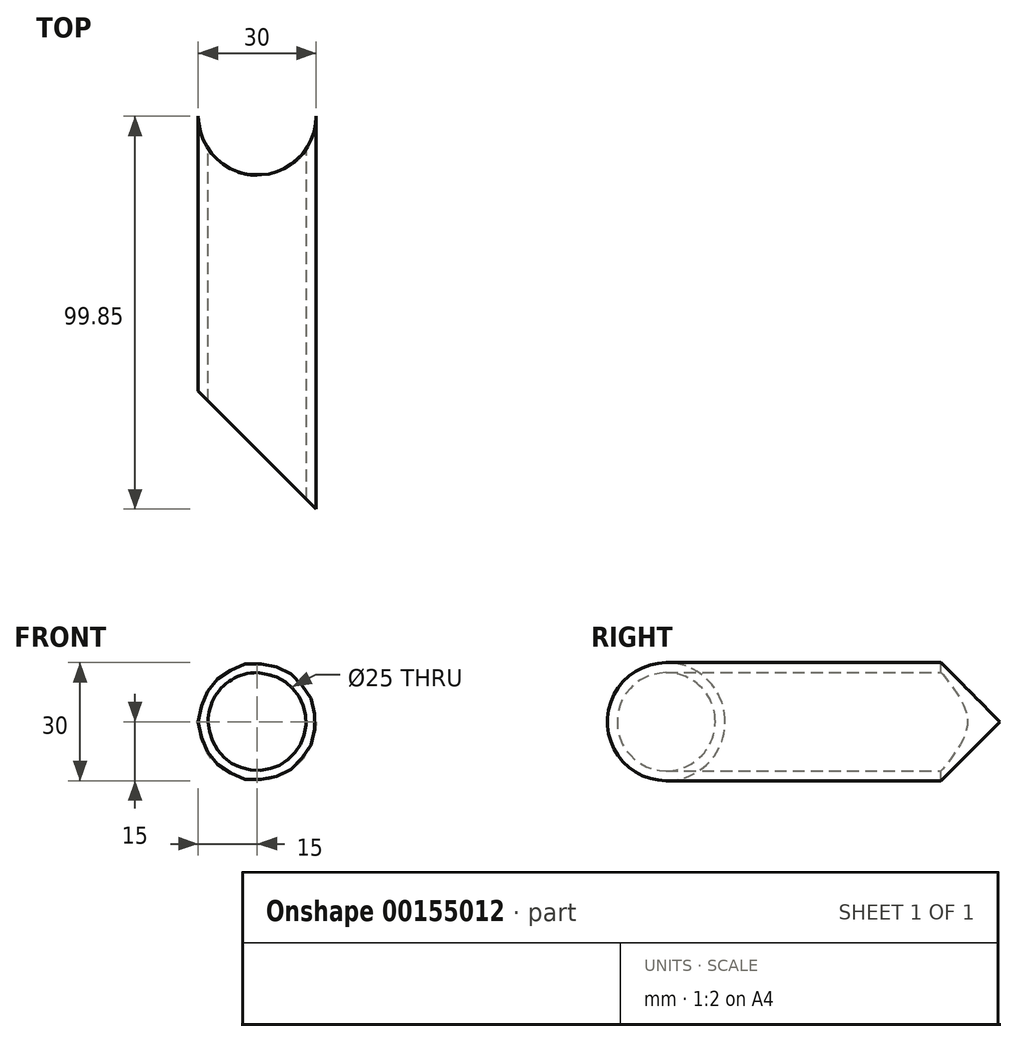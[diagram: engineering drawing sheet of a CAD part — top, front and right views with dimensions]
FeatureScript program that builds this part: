
annotation { "Feature Type Name" : "Feature", "Feature Type Description" : "" }
export const myFeature = defineFeature(function(context is Context, id is Id, definition is map)
    precondition{}
    {
        {
            var Q0;
            Q0=qCreatedBy(makeId("Front.planeOp"),FACE);
            var sketch = newSketch(context, id + "F0", { "sketchPlane" : qUnion([Q0])});
            skCircle(sketch, "E0", {"center": v(0, 0) * mm, "radius": 15 * mm});
            skCircle(sketch, "E1", {"center": v(0, 0) * mm, "radius": 12.5 * mm});
            skSolve(sketch);
        }
        {
            var Q0;
            Q0 = qSketchRegion(id + "F0", true);
            extrude(context, id + "F1", {"entities" : qUnion([Q0]), "depth" : 99.85 * mm});
        }
        {
            var Q0;
            Q0=qCreatedBy(makeId("Top.planeOp"),FACE);
            var sketch = newSketch(context, id + "F2", { "sketchPlane" : qUnion([Q0])});
            skCircle(sketch, "E2", {"center": v(0, 0) * mm, "radius": 15 * mm});
            skSolve(sketch);
        }
        {
            var Q0;
            Q0 = qSketchRegion(id + "F2", true);
            extrude(context, id + "F3", {"entities" : qUnion([Q0]), "operationType" : NewBodyOperationType.REMOVE, "endBound" : BoundingType.SYMMETRIC, "oppositeDirection" : true, "depth" : 35 * mm});
        }
        {
            var Q0;
            Q0=qCreatedBy(makeId("Top.planeOp"),FACE);
            var sketch = newSketch(context, id + "F4", { "sketchPlane" : qUnion([Q0])});
            skLineSegment(sketch, "E3.0", {"start": v(15, -99.85) * mm, "end": v(-15, -99.85) * mm});
            skLineSegment(sketch, "E4", {"start": v(15, -99.85) * mm, "end": v(-15, -69.85) * mm});
            skLineSegment(sketch, "E5", {"start": v(-15, -99.85) * mm, "end": v(-15, -69.85) * mm});
            skSolve(sketch);
        }
        {
            var Q0;
            Q0 = qSketchRegion(id + "F4", true);
            extrude(context, id + "F5", {"entities" : qUnion([Q0]), "operationType" : NewBodyOperationType.REMOVE, "endBound" : BoundingType.SYMMETRIC, "oppositeDirection" : true, "depth" : 35000 * mm});
        }
    });
